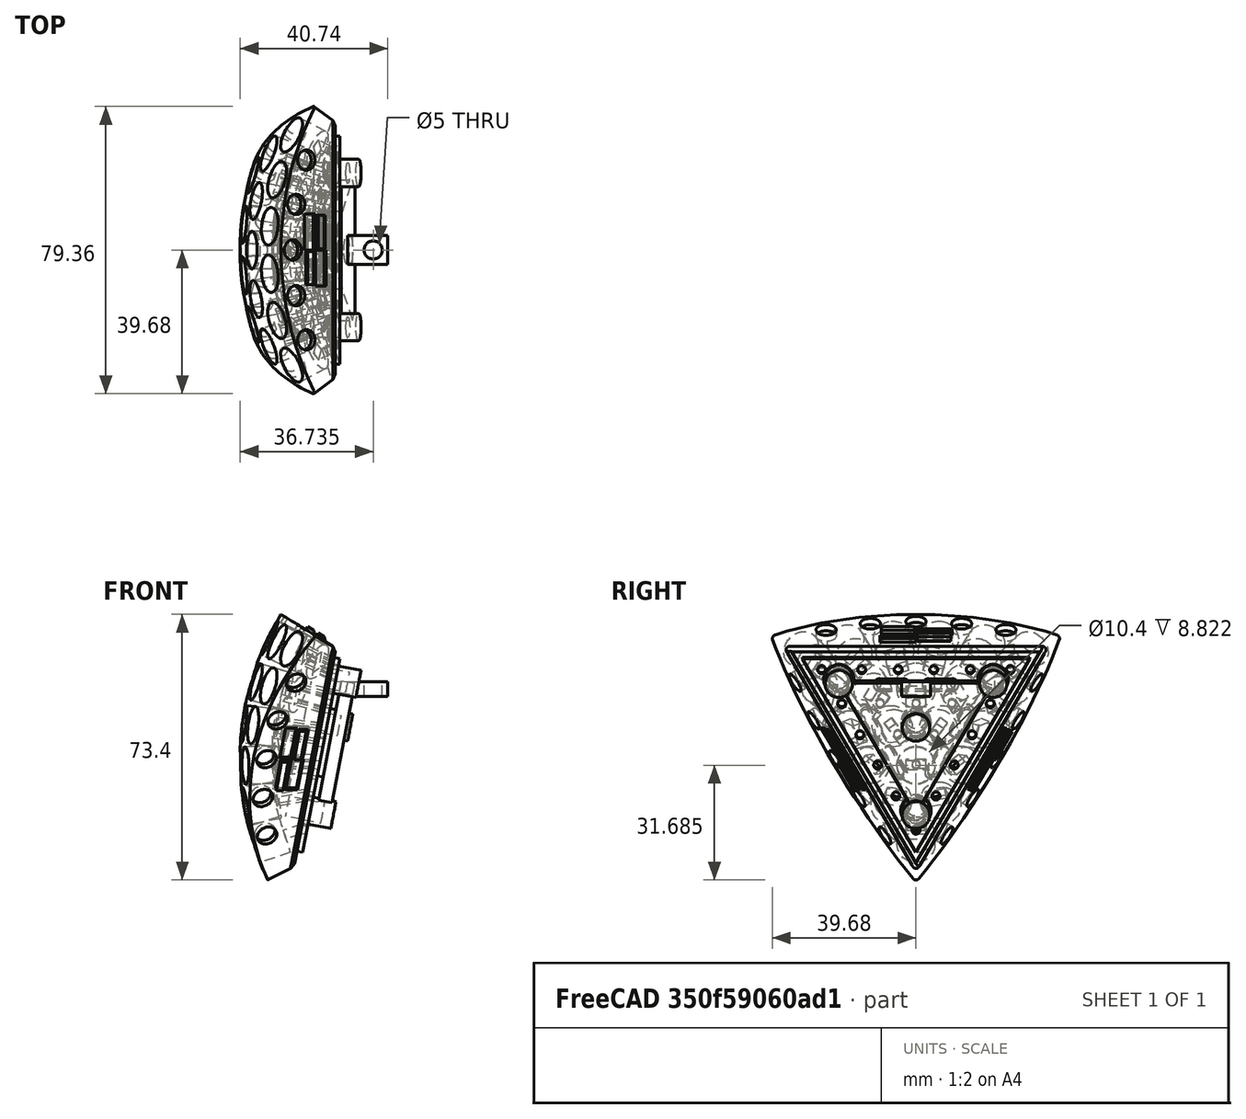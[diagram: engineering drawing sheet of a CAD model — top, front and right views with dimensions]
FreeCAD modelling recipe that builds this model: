
FCSTD DOCUMENT  (FreeCAD 0.20R27422 (Git))
Label: Shell_rev1
License: All rights reserved
LicenseURL: http://en.wikipedia.org/wiki/All_rights_reserved
objects: PartDesign::CoordinateSystem×9, Part::Feature×3, Part::Chamfer×3, Part::Part2DObjectPython×1, Part::Fillet×1, PartDesign::FeatureBase×1, PartDesign::Body×1
note: 19 computed .brp shape members not serialized (recipe doc carries the construction recipe); baked Part::Feature solids carry a one-line shape summary decoded from their .brp

FEATURE [Part::Part2DObjectPython] Line  # Draft 2D object (typed FeaturePython)
  Area = 0
  ChamferSize = 0
  Closed = false
  End = (-60.4609,0,-2.48e-14)
  FilletRadius = 0
  Length = 60.4609
  MakeFace = true
  Points = (2) [(0,0,0),(-60.4609,0,-2.4803e-14)]
  Start = (0,0,0)
  Subdivisions = 0
FEATURE [Part::Feature] Shape
  Placement = pos=(0,0,0) rot=(0,1,0;0.188711rad)
  shape: bbox 26.49 x 83.96 x 75.99 mm, 229 faces (baked)
FEATURE [Part::Feature] Shape001
  Placement = pos=(0,0,0) rot=(0,1,0;0.188711rad)
  shape: bbox 11.8 x 62.95 x 53.85 mm, 54 faces (baked)
FEATURE [Part::Feature] Shape002
  shape: bbox 23.55 x 50.22 x 45.22 mm, 59 faces (baked)
FEATURE [Part::Fillet] Fillet
  Base = -> Shape
  Edges = 3 edges r=1: [Edge25,Edge27,Edge50]
FEATURE [Part::Chamfer] Chamfer
  Base = -> Fillet
  Edges = 1 edges r=1: [Edge79]
FEATURE [Part::Chamfer] Chamfer001
  Base = -> Chamfer
  Edges = 4 edges r=0.4: [Edge150,Edge171,Edge184,Edge225]
FEATURE [Part::Chamfer] Chamfer002  label="shell"
  Base = -> Chamfer001
  Edges = 6 edges r=0.8: [Edge443,Edge453,Edge487,Edge499,Edge530,Edge542]
FEATURE [PartDesign::FeatureBase] BaseFeature
  BaseFeature = -> Chamfer002
FEATURE [PartDesign::CoordinateSystem] Local_CS
  AttacherType = Attacher::AttachEngine3D
  MapMode = 11
  Placement = pos=(-61.4889,-9e-15,38.0022) rot=(0.693258,0.693258,-0.19694;3.5305rad)
  Support = -> [BaseFeature]
FEATURE [PartDesign::CoordinateSystem] Local_CS001
  AttacherType = Attacher::AttachEngine3D
  MapMode = 11
  Placement = pos=(-68.7467,22.3371,-2.28e-14) rot=(0.459079,0.33354,-0.823406;2.06334rad)
  Support = -> [BaseFeature]
FEATURE [PartDesign::CoordinateSystem] Local_CS002
  AttacherType = Attacher::AttachEngine3D
  MapMode = 11
  Placement = pos=(-68.7467,-22.3371,-2.13e-14) rot=(-0.404509,-0.556759,-0.725529;1.57219rad)
  Support = -> [BaseFeature]
FEATURE [PartDesign::CoordinateSystem] Local_CS003
  AttacherType = Attacher::AttachEngine3D
  MapMode = 11
  Placement = pos=(-57.7484,-24.8267,35.6905) rot=(0.693258,0.693258,-0.19694;3.5305rad)
  Support = -> [BaseFeature]
FEATURE [PartDesign::CoordinateSystem] Local_CS004
  AttacherType = Attacher::AttachEngine3D
  MapMode = 11
  Placement = pos=(-68.598,-8.56496,-21.1189) rot=(-0.404509,-0.556759,-0.725529;1.57219rad)
  Support = -> [BaseFeature]
FEATURE [PartDesign::CoordinateSystem] Local_CS005
  AttacherType = Attacher::AttachEngine3D
  MapMode = 11
  Placement = pos=(-60.5313,33.3917,21.1189) rot=(0.459079,0.33354,-0.823406;2.06334rad)
  Support = -> [BaseFeature]
FEATURE [PartDesign::CoordinateSystem] Local_CS006
  AttacherType = Attacher::AttachEngine3D
  MapMode = 11
  Placement = pos=(-57.7484,24.8267,35.6905) rot=(0.693258,0.693258,-0.19694;3.5305rad)
  Support = -> [BaseFeature]
FEATURE [PartDesign::CoordinateSystem] Local_CS007
  AttacherType = Attacher::AttachEngine3D
  MapMode = 11
  Placement = pos=(-60.5313,-33.3917,21.1189) rot=(-0.404509,-0.556759,-0.725529;1.57219rad)
  Support = -> [BaseFeature]
FEATURE [PartDesign::CoordinateSystem] Local_CS008
  AttacherType = Attacher::AttachEngine3D
  MapMode = 11
  Placement = pos=(-68.598,8.56496,-21.1189) rot=(0.459079,0.33354,-0.823406;2.06334rad)
  Support = -> [BaseFeature]
FEATURE [PartDesign::Body] Body
  BaseFeature = -> Chamfer002
  Group = -> [BaseFeature,Local_CS,Local_CS001,Local_CS002,Local_CS003,Local_CS004,Local_CS005,Local_CS006,Local_CS007,Local_CS008]
  Origin = -> Origin
  Tip = -> BaseFeature
